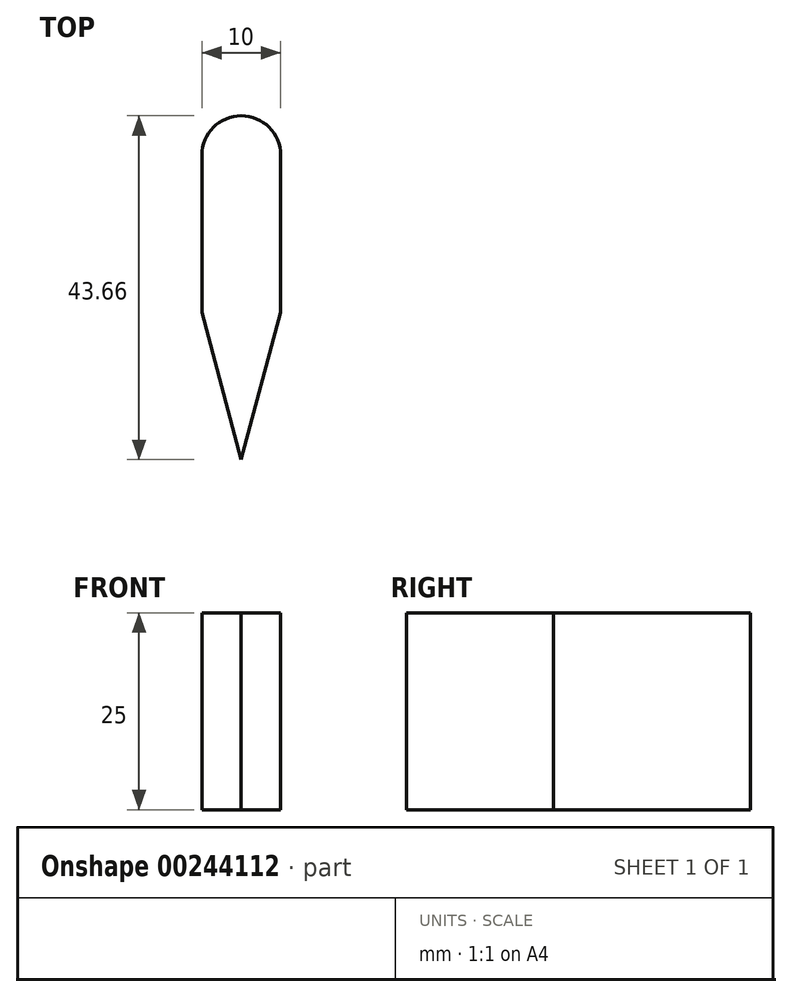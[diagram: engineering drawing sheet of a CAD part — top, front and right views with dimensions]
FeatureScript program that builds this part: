
annotation { "Feature Type Name" : "Feature", "Feature Type Description" : "" }
export const myFeature = defineFeature(function(context is Context, id is Id, definition is map)
    precondition{}
    {
        {
            var Q0;
            Q0=qCreatedBy(makeId("Top.planeOp"),FACE);
            var sketch = newSketch(context, id + "F0", { "sketchPlane" : qUnion([Q0])});
            skLineSegment(sketch, "E0.bottom", {"start": v(5, 10) * mm, "end": v(-5, 10) * mm});
            skLineSegment(sketch, "E0.top", {"start": v(5, -10) * mm, "end": v(-5, -10) * mm});
            skLineSegment(sketch, "E0.left", {"start": v(5, 10) * mm, "end": v(5, -10) * mm});
            skLineSegment(sketch, "E0.right", {"start": v(-5, 10) * mm, "end": v(-5, -10) * mm});
            skPoint(sketch, "E0.middle", {"position": v(0, 0) * mm});
            skArc(sketch, "E1", {"start": v(-5, 10) * mm, "mid": v(0, 15) * mm, "end": v(5, 10) * mm});
            skLineSegment(sketch, "E2", {"start": v(0, 0) * mm, "end": v(0, -57.32) * mm, "construction": true});
            skPoint(sketch, "E2.endSnap0", {"position": v(0, -10) * mm});
            skLineSegment(sketch, "E3", {"start": v(-5, -10) * mm, "end": v(0, -28.66) * mm});
            skLineSegment(sketch, "E4", {"start": v(0, -28.66) * mm, "end": v(5, -10) * mm});
            skSolve(sketch);
        }
        {
            var Q0;
            Q0=makeQuery(id+"F0.imprint","IMPRINT",FACE,{"disambiguationData":[TD([[makeQuery(id+"F0.imprint","IMPRINT",EDGE,{"derivedFrom":sQuery(id+"F0.wireOp",EDGE,"E0.bottom")}),1.0]])]});
            var Q1;
            Q1=makeQuery(id+"F0.imprint","IMPRINT",FACE,{"disambiguationData":[TD([[makeQuery(id+"F0.imprint","IMPRINT",EDGE,{"derivedFrom":sQuery(id+"F0.wireOp",EDGE,"E0.top")}),1.0]])]});
            var Q2;
            Q2=makeQuery(id+"F0.imprint","IMPRINT",FACE,{"disambiguationData":[TD([[makeQuery(id+"F0.imprint","IMPRINT",EDGE,{"derivedFrom":sQuery(id+"F0.wireOp",EDGE,"E0.bottom")}),-1.0]])]});
            extrude(context, id + "F1", {"entities" : qUnion([Q0, Q1, Q2]), "depth" : 25 * mm});
        }
    });
